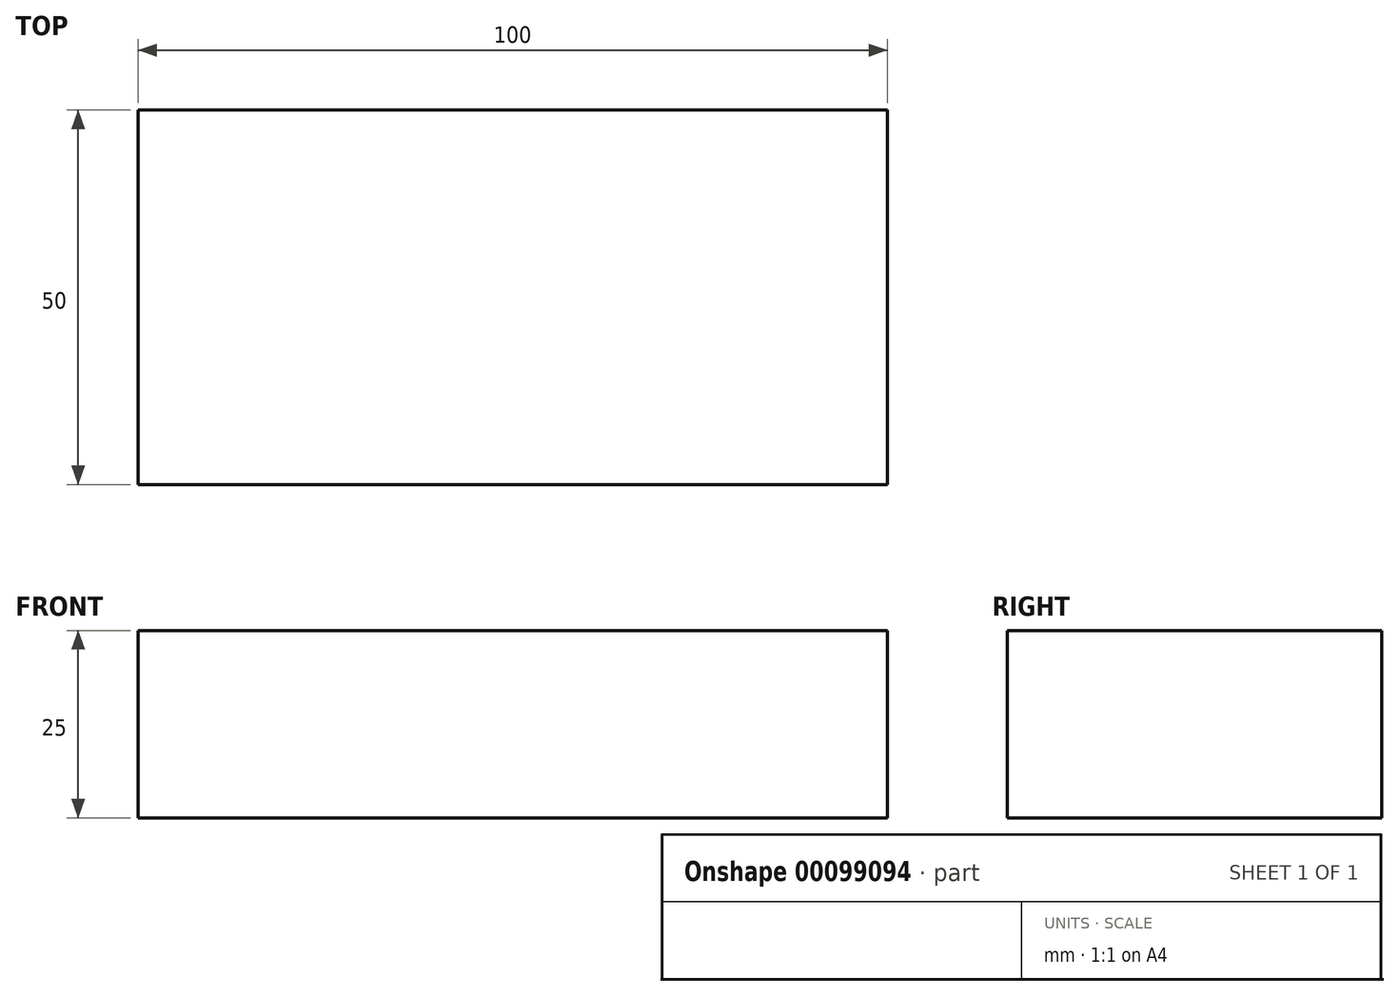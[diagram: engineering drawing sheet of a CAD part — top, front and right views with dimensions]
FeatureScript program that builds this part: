
annotation { "Feature Type Name" : "Feature", "Feature Type Description" : "" }
export const myFeature = defineFeature(function(context is Context, id is Id, definition is map)
    precondition{}
    {
        {
            var Q0;
            Q0=qCreatedBy(makeId("Top.planeOp"),FACE);
            var sketch = newSketch(context, id + "F0", { "sketchPlane" : qUnion([Q0])});
            skLineSegment(sketch, "E0.bottom", {"start": v(-100, 50) * mm, "end": v(0, 50) * mm});
            skLineSegment(sketch, "E0.top", {"start": v(-100, 0) * mm, "end": v(0, 0) * mm});
            skLineSegment(sketch, "E0.left", {"start": v(-100, 50) * mm, "end": v(-100, 0) * mm});
            skLineSegment(sketch, "E0.right", {"start": v(0, 50) * mm, "end": v(0, 0) * mm});
            skSolve(sketch);
        }
        {
            var Q0;
            Q0=makeQuery(id+"F0.imprint","IMPRINT",FACE,{"disambiguationData":[TD([[makeQuery(id+"F0.imprint","IMPRINT",EDGE,{"derivedFrom":sQuery(id+"F0.wireOp",EDGE,"E0.bottom")}),-1.0]])]});
            extrude(context, id + "F1", {"entities" : qUnion([Q0]), "depth" : 25 * mm});
        }
    });
